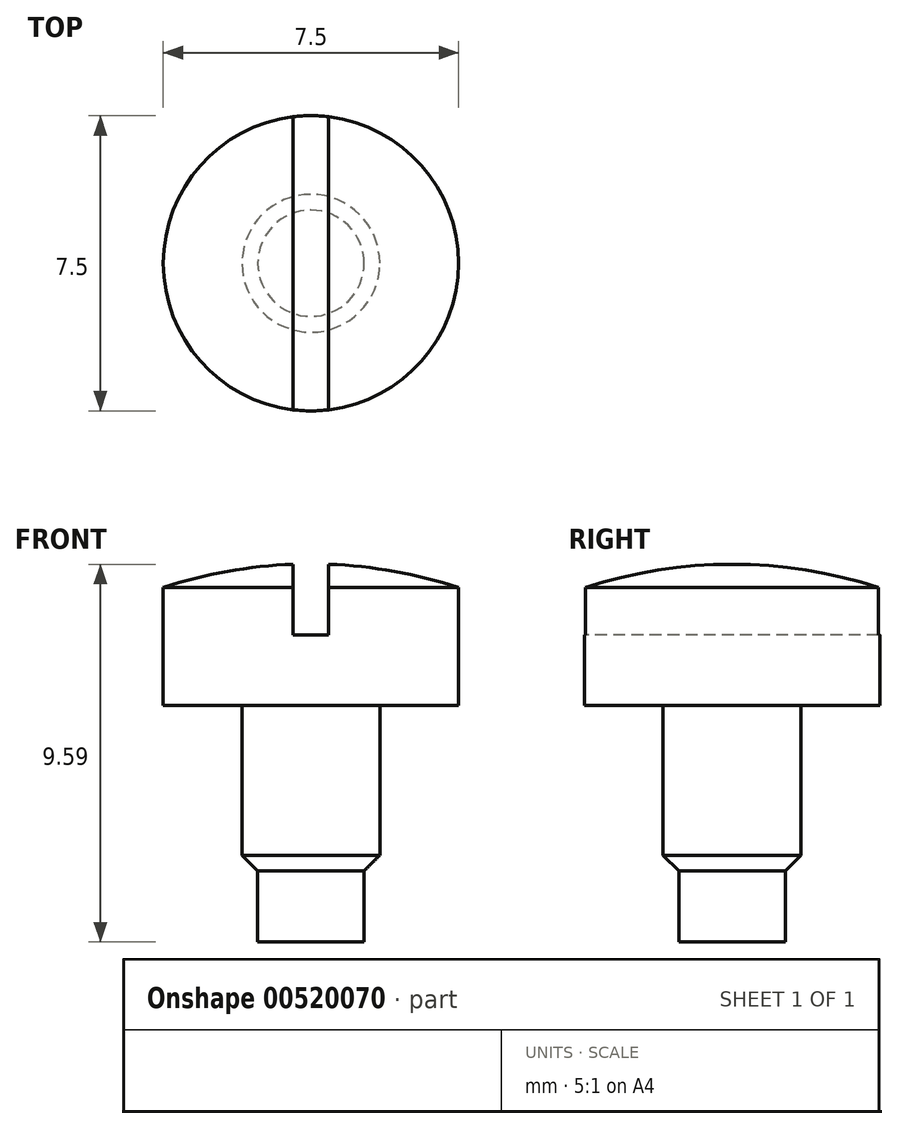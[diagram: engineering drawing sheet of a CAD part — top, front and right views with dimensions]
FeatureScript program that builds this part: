
annotation { "Feature Type Name" : "Feature", "Feature Type Description" : "" }
export const myFeature = defineFeature(function(context is Context, id is Id, definition is map)
    precondition{}
    {
        {
            var Q0;
            Q0=qCreatedBy(makeId("Front.planeOp"),FACE);
            var sketch = newSketch(context, id + "F0", { "sketchPlane" : qUnion([Q0])});
            skLineSegment(sketch, "E0", {"start": v(0, 0) * mm, "end": v(0.45, 0) * mm});
            skLineSegment(sketch, "E1", {"start": v(0.45, 0) * mm, "end": v(0.45, 0.6) * mm});
            skLineSegment(sketch, "E2", {"start": v(0.45, 0.6) * mm, "end": v(0.58, 0.73) * mm});
            skLineSegment(sketch, "E3", {"start": v(0.58, 0.73) * mm, "end": v(0.58, 2) * mm});
            skLineSegment(sketch, "E4", {"start": v(0.58, 2) * mm, "end": v(1.25, 2) * mm});
            skLineSegment(sketch, "E5", {"start": v(1.25, 2) * mm, "end": v(1.25, 3) * mm});
            skLineSegment(sketch, "E6", {"start": v(1.25, 3) * mm, "end": v(0, 3) * mm});
            skLineSegment(sketch, "E7", {"start": v(0, 3) * mm, "end": v(0, 0) * mm});
            skArc(sketch, "E8", {"start": v(1.25, 3) * mm, "mid": v(0.63, 3.15) * mm, "end": v(0, 3.2) * mm});
            skLineSegment(sketch, "E9", {"start": v(0, 3.2) * mm, "end": v(0, 3) * mm});
            skSolve(sketch);
        }
        {
            var Q0;
            {var subQ0=makeQuery(id+"F0.imprint","IMPRINT",EDGE,{"derivedFrom":sQuery(id+"F0.wireOp",EDGE,"E6")});Q0=qUnion([makeQuery(id+"F0.imprint","IMPRINT",FACE,{"disambiguationData":[TD([[makeQuery(id+"F0.imprint","IMPRINT",EDGE,{"derivedFrom":sQuery(id+"F0.wireOp",EDGE,"E0")}),1.0]])]}),makeQuery(id+"F0.imprint","IMPRINT",FACE,{"disambiguationData":[TD([[subQ0,-1.0]])]})]);}
            var Q1;
            Q1=sQuery(id+"F0.wireOp",EDGE,"E7");
            revolve(context, id + "F1", {"entities" : qUnion([Q0]), "axis" : qUnion([Q1]), "revolveType" : RevolveType.FULL});
        }
        {
            var Q0;
            Q0=qCreatedBy(makeId("Front.planeOp"),FACE);
            var sketch = newSketch(context, id + "F2", { "sketchPlane" : qUnion([Q0])});
            skLineSegment(sketch, "E10", {"start": v(-0.15, 2.6) * mm, "end": v(0.15, 2.6) * mm});
            skPoint(sketch, "E11", {"position": v(0, 2.6) * mm});
            skLineSegment(sketch, "E12", {"start": v(-0.15, 2.6) * mm, "end": v(-0.15, 3.25) * mm});
            skLineSegment(sketch, "E13", {"start": v(-0.15, 3.25) * mm, "end": v(0.15, 3.25) * mm});
            skLineSegment(sketch, "E14", {"start": v(0.15, 3.25) * mm, "end": v(0.15, 2.6) * mm});
            skSolve(sketch);
        }
        {
            var Q0;
            Q0=makeQuery(id+"F2.imprint","IMPRINT",FACE,{"disambiguationData":[TD([[makeQuery(id+"F2.imprint","IMPRINT",EDGE,{"derivedFrom":sQuery(id+"F2.wireOp",EDGE,"E10")}),1.0]])]});
            extrude(context, id + "F3", {"entities" : qUnion([Q0]), "operationType" : NewBodyOperationType.REMOVE, "endBound" : BoundingType.SYMMETRIC, "oppositeDirection" : true, "depth" : 25 * mm});
        }
        {
            var Q0;
            Q0=makeQuery(id+"F1.opRevolve","SWEPT_BODY",BODY,{"disambiguationData":[OSD([sQuery(id+"F0.wireOp",EDGE,"E0"),sQuery(id+"F0.wireOp",EDGE,"E1"),sQuery(id+"F0.wireOp",EDGE,"E2"),sQuery(id+"F0.wireOp",EDGE,"E3"),sQuery(id+"F0.wireOp",EDGE,"E4"),sQuery(id+"F0.wireOp",EDGE,"E5"),sQuery(id+"F0.wireOp",EDGE,"E7"),sQuery(id+"F0.wireOp",EDGE,"E8"),sQuery(id+"F0.wireOp",EDGE,"E9")])]});
            var Q1;
            Q1=qCreatedBy(makeId("Origin.pointOp"),VERTEX);
            transform(context, id + "F4", {"entities" : qUnion([Q0]), "transformType" : TransformType.SCALE_UNIFORMLY, "scale" : 3, "makeCopy" : false, "scalePoint" : qUnion([Q1])});
        }
    });
